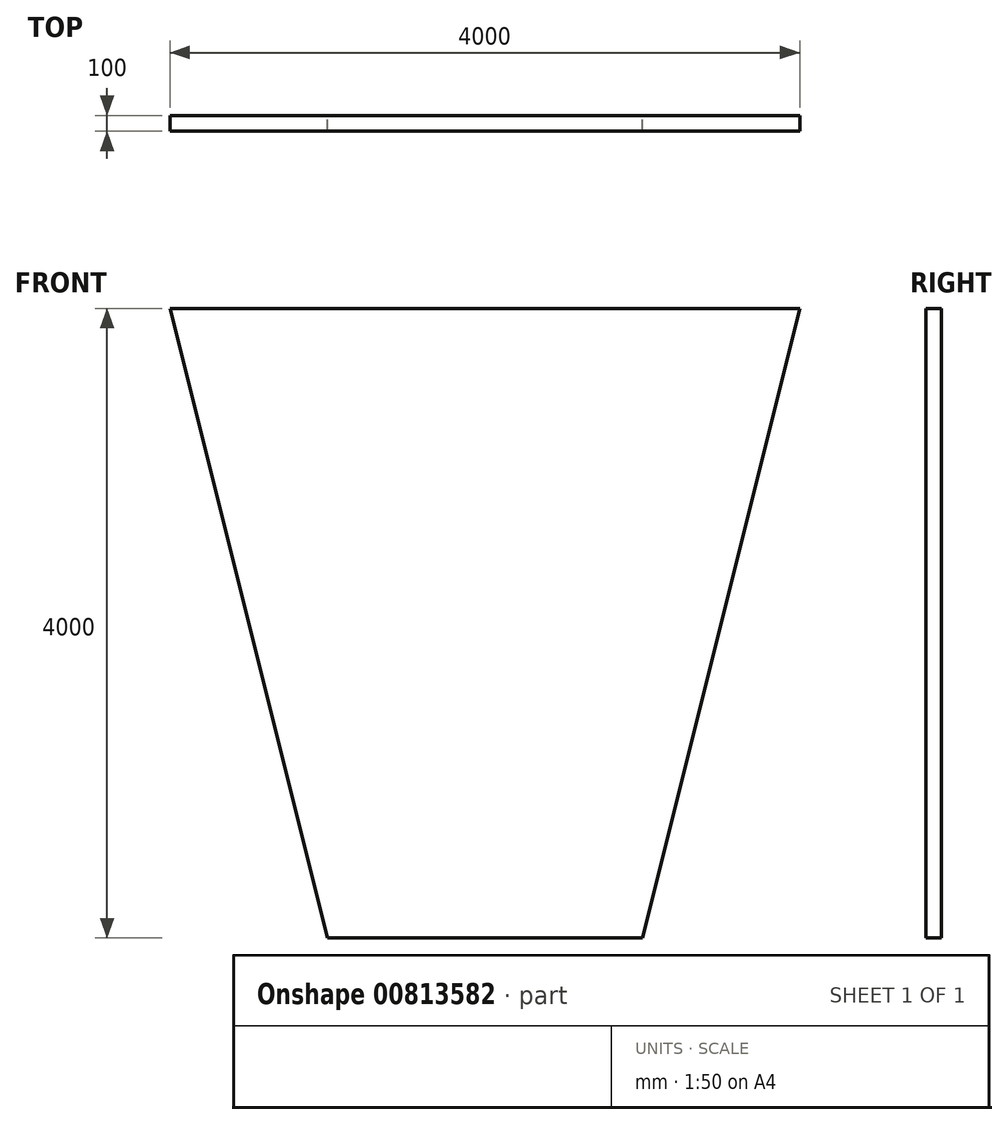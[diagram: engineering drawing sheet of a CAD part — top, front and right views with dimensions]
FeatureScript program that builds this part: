
annotation { "Feature Type Name" : "Feature", "Feature Type Description" : "" }
export const myFeature = defineFeature(function(context is Context, id is Id, definition is map)
    precondition{}
    {
        {
            var Q0;
            Q0=qCreatedBy(makeId("Front.planeOp"),FACE);
            var sketch = newSketch(context, id + "F0", { "sketchPlane" : qUnion([Q0])});
            skLineSegment(sketch, "E0", {"start": v(0, 247.2) * mm, "end": v(-2000, 247.2) * mm});
            skLineSegment(sketch, "E1", {"start": v(0, -3752.8) * mm, "end": v(-1000, -3752.8) * mm});
            skLineSegment(sketch, "E2", {"start": v(-2000, 247.2) * mm, "end": v(-1000, -3752.8) * mm});
            skLineSegment(sketch, "E3.MirrorCS", {"start": v(0, 247.2) * mm, "end": v(2000, 247.2) * mm});
            skLineSegment(sketch, "E4.MirrorCS", {"start": v(2000, 247.2) * mm, "end": v(1000, -3752.8) * mm});
            skLineSegment(sketch, "E5.MirrorCS", {"start": v(0, -3752.8) * mm, "end": v(1000, -3752.8) * mm});
            skSolve(sketch);
        }
        {
            var Q0;
            Q0=makeQuery(id+"F0.imprint","IMPRINT",FACE,{"disambiguationData":[TD([[makeQuery(id+"F0.imprint","IMPRINT",EDGE,{"derivedFrom":sQuery(id+"F0.wireOp",EDGE,"E0")}),1.0]])]});
            extrude(context, id + "F1", {"entities" : qUnion([Q0]), "depth" : 100 * mm, "offsetDistance" : 25 * mm});
        }
    });
